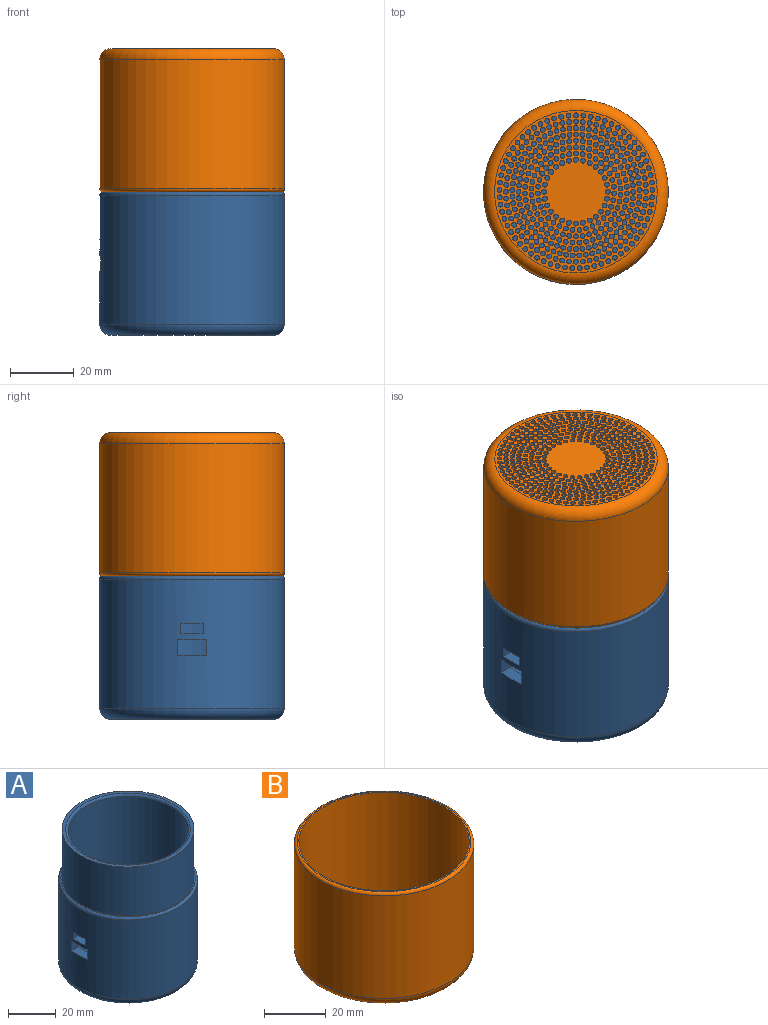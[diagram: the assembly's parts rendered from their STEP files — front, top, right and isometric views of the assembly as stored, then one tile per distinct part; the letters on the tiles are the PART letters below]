
ASSEMBLY  parts=2 mates=1
PART A: 18 faces, bbox 62.8x62.8x70 mm
  f0: cylinder r=29mm len=58mm, axis (0,0,-1), area 7312mm2, adj f6,f7,f8,f9,f10,f11,f12,f13
  f1: plane 55x55mm, normal (0,0,1), area 252.1mm2, adj f5,f15
  f2: cylinder r=25mm len=59mm, axis (0,0,1), area 9200mm2, adj f4,f5,f6,f7,f8,f9,f10,f11
  f3: plane 51x51mm, normal (0,0,-1), area 2042.8mm2, adj f17
  f4: plane 50x50mm, normal (0,0,1), area 1963.5mm2, adj f2
  f5: torus R=26mm, axis (0,0,1), area 250.3mm2, adj f1,f2
  f6: plane 9x4.41mm, normal (0,0,-1), area 36.2mm2, adj f0,f2,f7,f9
  f7: plane 5x4.06mm, normal (0,1,0), area 20.3mm2, adj f0,f2,f6,f8
  f8: plane 9x4.41mm, normal (0,0,1), area 36.2mm2, adj f0,f2,f7,f9
  f9: plane 5x4.06mm, normal (0,-1,0), area 20.3mm2, adj f0,f2,f6,f8
  f10: plane 4.03x3.2mm, normal (0,-1,0), area 12.9mm2, adj f0,f2,f11,f13
  f11: plane 7x4.25mm, normal (0,0,-1), area 28.1mm2, adj f0,f2,f10,f12
  f12: plane 4.03x3.2mm, normal (0,1,0), area 12.9mm2, adj f0,f2,f11,f13
  f13: plane 7x4.25mm, normal (0,0,1), area 28.1mm2, adj f0,f2,f10,f12
  f14: plane 56x56mm, normal (0,0,1), area 87.2mm2, adj f15,f16
  f15: cylinder r=27.5mm len=55mm, axis (0,0,1), area 4319.7mm2, adj f1,f14
  f16: torus R=28mm, axis (0,0,1), area 282.6mm2, adj f0,f14
  f17: torus R=25.5mm, axis (0,0,1), area 957.8mm2, adj f0,f3
PART B: 409 faces, bbox 62.8x62.8x45 mm
  f0: plane 51x51mm, normal (0,0,1), area 1339.5mm2, adj f6,f7,f8,f9,f10,f11,f12,f13
  f1: cylinder r=29mm len=58mm, axis (0,0,-1), area 7379.6mm2, adj f407,f408
  f2: plane 56x56mm, normal (0,0,1), area 87.2mm2, adj f4,f408
  f3: plane 51x51mm, normal (0,0,-1), area 1339.5mm2, adj f6,f7,f8,f9,f10,f11,f12,f13
  f4: cylinder r=27.5mm len=55mm, axis (0,0,1), area 6911.5mm2, adj f2,f5
  f5: plane 55x55mm, normal (0,0,1), area 43mm2, adj f4,f405
  f6: cylinder r=0.75mm len=5mm, axis (0,0,-1), area 23.6mm2, adj f0,f3
  f7: cylinder r=0.75mm len=5mm, axis (0,0,-1), area 23.6mm2, adj f0,f3
  f8: cylinder r=0.75mm len=5mm, axis (0,0,-1), area 23.6mm2, adj f0,f3
  f9: cylinder r=0.75mm len=5mm, axis (0,0,-1), area 23.6mm2, adj f0,f3
  f10: cylinder r=0.75mm len=5mm, axis (0,0,-1), area 23.6mm2, adj f0,f3
  f11: cylinder r=0.75mm len=5mm, axis (0,0,-1), area 23.6mm2, adj f0,f3
  f12: cylinder r=0.75mm len=5mm, axis (0,0,-1), area 23.6mm2, adj f0,f3
  f13: cylinder r=0.75mm len=5mm, axis (0,0,-1), area 23.6mm2, adj f0,f3
  f14: cylinder r=0.75mm len=5mm, axis (0,0,-1), area 23.6mm2, adj f0,f3
  f15: cylinder r=0.75mm len=5mm, axis (0,0,-1), area 23.6mm2, adj f0,f3
  f16: cylinder r=0.75mm len=5mm, axis (0,0,-1), area 23.6mm2, adj f0,f3
  f17: cylinder r=0.75mm len=5mm, axis (0,0,-1), area 23.6mm2, adj f0,f3
  f18: cylinder r=0.75mm len=5mm, axis (0,0,-1), area 23.6mm2, adj f0,f3
  f19: cylinder r=0.75mm len=5mm, axis (0,0,-1), area 23.6mm2, adj f0,f3
  f20: cylinder r=0.75mm len=5mm, axis (0,0,-1), area 23.6mm2, adj f0,f3
  f21: cylinder r=0.75mm len=5mm, axis (0,0,-1), area 23.6mm2, adj f0,f3
  f22: cylinder r=0.75mm len=5mm, axis (0,0,-1), area 23.6mm2, adj f0,f3
  f23: cylinder r=0.75mm len=5mm, axis (0,0,-1), area 23.6mm2, adj f0,f3
  f24: cylinder r=0.75mm len=5mm, axis (0,0,-1), area 23.6mm2, adj f0,f3
  f25: cylinder r=0.75mm len=5mm, axis (0,0,-1), area 23.6mm2, adj f0,f3
  f26: cylinder r=0.75mm len=5mm, axis (0,0,-1), area 23.6mm2, adj f0,f3
  f27: cylinder r=0.75mm len=5mm, axis (0,0,-1), area 23.6mm2, adj f0,f3
  f28: cylinder r=0.75mm len=5mm, axis (0,0,-1), area 23.6mm2, adj f0,f3
  f29: cylinder r=0.75mm len=5mm, axis (0,0,-1), area 23.6mm2, adj f0,f3
  f30: cylinder r=0.75mm len=5mm, axis (0,0,-1), area 23.6mm2, adj f0,f3
  f31: cylinder r=0.75mm len=5mm, axis (0,0,-1), area 23.6mm2, adj f0,f3
  f32: cylinder r=0.75mm len=5mm, axis (0,0,-1), area 23.6mm2, adj f0,f3
  f33: cylinder r=0.75mm len=5mm, axis (0,0,-1), area 23.6mm2, adj f0,f3
  f34: cylinder r=0.75mm len=5mm, axis (0,0,-1), area 23.6mm2, adj f0,f3
  f35: cylinder r=0.75mm len=5mm, axis (0,0,-1), area 23.6mm2, adj f0,f3
  f36: cylinder r=0.75mm len=5mm, axis (0,0,-1), area 23.6mm2, adj f0,f3
  f37: cylinder r=0.75mm len=5mm, axis (0,0,-1), area 23.6mm2, adj f0,f3
  f38: cylinder r=0.75mm len=5mm, axis (0,0,-1), area 23.6mm2, adj f0,f3
  f39: cylinder r=0.75mm len=5mm, axis (0,0,-1), area 23.6mm2, adj f0,f3
  f40: cylinder r=0.75mm len=5mm, axis (0,0,-1), area 23.6mm2, adj f0,f3
  f41: cylinder r=0.75mm len=5mm, axis (0,0,-1), area 23.6mm2, adj f0,f3
  f42: cylinder r=0.75mm len=5mm, axis (0,0,-1), area 23.6mm2, adj f0,f3
  f43: cylinder r=0.75mm len=5mm, axis (0,0,-1), area 23.6mm2, adj f0,f3
  f44: cylinder r=0.75mm len=5mm, axis (0,0,-1), area 23.6mm2, adj f0,f3
  f45: cylinder r=0.75mm len=5mm, axis (0,0,-1), area 23.6mm2, adj f0,f3
  f46: cylinder r=0.75mm len=5mm, axis (0,0,-1), area 23.6mm2, adj f0,f3
  f47: cylinder r=0.75mm len=5mm, axis (0,0,-1), area 23.6mm2, adj f0,f3
  f48: cylinder r=0.75mm len=5mm, axis (0,0,-1), area 23.6mm2, adj f0,f3
  f49: cylinder r=0.75mm len=5mm, axis (0,0,-1), area 23.6mm2, adj f0,f3
  f50: cylinder r=0.75mm len=5mm, axis (0,0,-1), area 23.6mm2, adj f0,f3
  f51: cylinder r=0.75mm len=5mm, axis (0,0,-1), area 23.6mm2, adj f0,f3
  f52: cylinder r=0.75mm len=5mm, axis (0,0,-1), area 23.6mm2, adj f0,f3
  f53: cylinder r=0.75mm len=5mm, axis (0,0,-1), area 23.6mm2, adj f0,f3
  f54: cylinder r=0.75mm len=5mm, axis (0,0,-1), area 23.6mm2, adj f0,f3
  f55: cylinder r=0.75mm len=5mm, axis (0,0,-1), area 23.6mm2, adj f0,f3
  f56: cylinder r=0.75mm len=5mm, axis (0,0,-1), area 23.6mm2, adj f0,f3
  f57: cylinder r=0.75mm len=5mm, axis (0,0,-1), area 23.6mm2, adj f0,f3
  f58: cylinder r=0.75mm len=5mm, axis (0,0,-1), area 23.6mm2, adj f0,f3
  f59: cylinder r=0.75mm len=5mm, axis (0,0,-1), area 23.6mm2, adj f0,f3
  f60: cylinder r=0.75mm len=5mm, axis (0,0,-1), area 23.6mm2, adj f0,f3
  f61: cylinder r=0.75mm len=5mm, axis (0,0,-1), area 23.6mm2, adj f0,f3
  f62: cylinder r=0.75mm len=5mm, axis (0,0,-1), area 23.6mm2, adj f0,f3
  f63: cylinder r=0.75mm len=5mm, axis (0,0,-1), area 23.6mm2, adj f0,f3
  f64: cylinder r=0.75mm len=5mm, axis (0,0,-1), area 23.6mm2, adj f0,f3
  f65: cylinder r=0.75mm len=5mm, axis (0,0,-1), area 23.6mm2, adj f0,f3
  f66: cylinder r=0.75mm len=5mm, axis (0,0,-1), area 23.6mm2, adj f0,f3
  f67: cylinder r=0.75mm len=5mm, axis (0,0,-1), area 23.6mm2, adj f0,f3
  f68: cylinder r=0.75mm len=5mm, axis (0,0,-1), area 23.6mm2, adj f0,f3
  f69: cylinder r=0.75mm len=5mm, axis (0,0,-1), area 23.6mm2, adj f0,f3
  f70: cylinder r=0.75mm len=5mm, axis (0,0,-1), area 23.6mm2, adj f0,f3
  f71: cylinder r=0.75mm len=5mm, axis (0,0,-1), area 23.6mm2, adj f0,f3
  f72: cylinder r=0.75mm len=5mm, axis (0,0,-1), area 23.6mm2, adj f0,f3
  f73: cylinder r=0.75mm len=5mm, axis (0,0,-1), area 23.6mm2, adj f0,f3
  f74: cylinder r=0.75mm len=5mm, axis (0,0,-1), area 23.6mm2, adj f0,f3
  f75: cylinder r=0.75mm len=5mm, axis (0,0,-1), area 23.6mm2, adj f0,f3
  f76: cylinder r=0.75mm len=5mm, axis (0,0,-1), area 23.6mm2, adj f0,f3
  f77: cylinder r=0.75mm len=5mm, axis (0,0,-1), area 23.6mm2, adj f0,f3
  f78: cylinder r=0.75mm len=5mm, axis (0,0,-1), area 23.6mm2, adj f0,f3
  f79: cylinder r=0.75mm len=5mm, axis (0,0,-1), area 23.6mm2, adj f0,f3
  f80: cylinder r=0.75mm len=5mm, axis (0,0,-1), area 23.6mm2, adj f0,f3
  f81: cylinder r=0.75mm len=5mm, axis (0,0,-1), area 23.6mm2, adj f0,f3
  f82: cylinder r=0.75mm len=5mm, axis (0,0,-1), area 23.6mm2, adj f0,f3
  f83: cylinder r=0.75mm len=5mm, axis (0,0,-1), area 23.6mm2, adj f0,f3
  f84: cylinder r=0.75mm len=5mm, axis (0,0,-1), area 23.6mm2, adj f0,f3
  f85: cylinder r=0.75mm len=5mm, axis (0,0,-1), area 23.6mm2, adj f0,f3
  f86: cylinder r=0.75mm len=5mm, axis (0,0,-1), area 23.6mm2, adj f0,f3
  f87: cylinder r=0.75mm len=5mm, axis (0,0,-1), area 23.6mm2, adj f0,f3
  f88: cylinder r=0.75mm len=5mm, axis (0,0,-1), area 23.6mm2, adj f0,f3
  f89: cylinder r=0.75mm len=5mm, axis (0,0,-1), area 23.6mm2, adj f0,f3
  f90: cylinder r=0.75mm len=5mm, axis (0,0,-1), area 23.6mm2, adj f0,f3
  f91: cylinder r=0.75mm len=5mm, axis (0,0,-1), area 23.6mm2, adj f0,f3
  f92: cylinder r=0.75mm len=5mm, axis (0,0,-1), area 23.6mm2, adj f0,f3
  f93: cylinder r=0.75mm len=5mm, axis (0,0,-1), area 23.6mm2, adj f0,f3
  f94: cylinder r=0.75mm len=5mm, axis (0,0,-1), area 23.6mm2, adj f0,f3
  f95: cylinder r=0.75mm len=5mm, axis (0,0,-1), area 23.6mm2, adj f0,f3
  f96: cylinder r=0.75mm len=5mm, axis (0,0,-1), area 23.6mm2, adj f0,f3
  f97: cylinder r=0.75mm len=5mm, axis (0,0,-1), area 23.6mm2, adj f0,f3
  f98: cylinder r=0.75mm len=5mm, axis (0,0,-1), area 23.6mm2, adj f0,f3
  f99: cylinder r=0.75mm len=5mm, axis (0,0,-1), area 23.6mm2, adj f0,f3
  f100: cylinder r=0.75mm len=5mm, axis (0,0,-1), area 23.6mm2, adj f0,f3
  f101: cylinder r=0.75mm len=5mm, axis (0,0,-1), area 23.6mm2, adj f0,f3
  f102: cylinder r=0.75mm len=5mm, axis (0,0,-1), area 23.6mm2, adj f0,f3
  f103: cylinder r=0.75mm len=5mm, axis (0,0,-1), area 23.6mm2, adj f0,f3
  f104: cylinder r=0.75mm len=5mm, axis (0,0,-1), area 23.6mm2, adj f0,f3
  f105: cylinder r=0.75mm len=5mm, axis (0,0,-1), area 23.6mm2, adj f0,f3
  f106: cylinder r=0.75mm len=5mm, axis (0,0,-1), area 23.6mm2, adj f0,f3
  f107: cylinder r=0.75mm len=5mm, axis (0,0,-1), area 23.6mm2, adj f0,f3
  f108: cylinder r=0.75mm len=5mm, axis (0,0,-1), area 23.6mm2, adj f0,f3
  f109: cylinder r=0.75mm len=5mm, axis (0,0,-1), area 23.6mm2, adj f0,f3
  f110: cylinder r=0.75mm len=5mm, axis (0,0,-1), area 23.6mm2, adj f0,f3
  f111: cylinder r=0.75mm len=5mm, axis (0,0,-1), area 23.6mm2, adj f0,f3
  f112: cylinder r=0.75mm len=5mm, axis (0,0,-1), area 23.6mm2, adj f0,f3
  f113: cylinder r=0.75mm len=5mm, axis (0,0,-1), area 23.6mm2, adj f0,f3
  f114: cylinder r=0.75mm len=5mm, axis (0,0,-1), area 23.6mm2, adj f0,f3
  f115: cylinder r=0.75mm len=5mm, axis (0,0,-1), area 23.6mm2, adj f0,f3
  f116: cylinder r=0.75mm len=5mm, axis (0,0,-1), area 23.6mm2, adj f0,f3
  f117: cylinder r=0.75mm len=5mm, axis (0,0,-1), area 23.6mm2, adj f0,f3
  f118: cylinder r=0.75mm len=5mm, axis (0,0,-1), area 23.6mm2, adj f0,f3
  f119: cylinder r=0.75mm len=5mm, axis (0,0,-1), area 23.6mm2, adj f0,f3
  f120: cylinder r=0.75mm len=5mm, axis (0,0,-1), area 23.6mm2, adj f0,f3
  f121: cylinder r=0.75mm len=5mm, axis (0,0,-1), area 23.6mm2, adj f0,f3
  f122: cylinder r=0.75mm len=5mm, axis (0,0,-1), area 23.6mm2, adj f0,f3
  f123: cylinder r=0.75mm len=5mm, axis (0,0,-1), area 23.6mm2, adj f0,f3
  f124: cylinder r=0.75mm len=5mm, axis (0,0,-1), area 23.6mm2, adj f0,f3
  f125: cylinder r=0.75mm len=5mm, axis (0,0,-1), area 23.6mm2, adj f0,f3
  f126: cylinder r=0.75mm len=5mm, axis (0,0,-1), area 23.6mm2, adj f0,f3
  f127: cylinder r=0.75mm len=5mm, axis (0,0,-1), area 23.6mm2, adj f0,f3
  f128: cylinder r=0.75mm len=5mm, axis (0,0,-1), area 23.6mm2, adj f0,f3
  f129: cylinder r=0.75mm len=5mm, axis (0,0,-1), area 23.6mm2, adj f0,f3
  f130: cylinder r=0.75mm len=5mm, axis (0,0,-1), area 23.6mm2, adj f0,f3
  f131: cylinder r=0.75mm len=5mm, axis (0,0,-1), area 23.6mm2, adj f0,f3
  f132: cylinder r=0.75mm len=5mm, axis (0,0,-1), area 23.6mm2, adj f0,f3
  f133: cylinder r=0.75mm len=5mm, axis (0,0,-1), area 23.6mm2, adj f0,f3
  f134: cylinder r=0.75mm len=5mm, axis (0,0,-1), area 23.6mm2, adj f0,f3
  f135: cylinder r=0.75mm len=5mm, axis (0,0,-1), area 23.6mm2, adj f0,f3
  f136: cylinder r=0.75mm len=5mm, axis (0,0,-1), area 23.6mm2, adj f0,f3
  f137: cylinder r=0.75mm len=5mm, axis (0,0,-1), area 23.6mm2, adj f0,f3
  f138: cylinder r=0.75mm len=5mm, axis (0,0,-1), area 23.6mm2, adj f0,f3
  f139: cylinder r=0.75mm len=5mm, axis (0,0,-1), area 23.6mm2, adj f0,f3
  f140: cylinder r=0.75mm len=5mm, axis (0,0,-1), area 23.6mm2, adj f0,f3
  f141: cylinder r=0.75mm len=5mm, axis (0,0,-1), area 23.6mm2, adj f0,f3
  f142: cylinder r=0.75mm len=5mm, axis (0,0,-1), area 23.6mm2, adj f0,f3
  f143: cylinder r=0.75mm len=5mm, axis (0,0,-1), area 23.6mm2, adj f0,f3
  f144: cylinder r=0.75mm len=5mm, axis (0,0,-1), area 23.6mm2, adj f0,f3
  f145: cylinder r=0.75mm len=5mm, axis (0,0,-1), area 23.6mm2, adj f0,f3
  f146: cylinder r=0.75mm len=5mm, axis (0,0,-1), area 23.6mm2, adj f0,f3
  f147: cylinder r=0.75mm len=5mm, axis (0,0,-1), area 23.6mm2, adj f0,f3
  f148: cylinder r=0.75mm len=5mm, axis (0,0,-1), area 23.6mm2, adj f0,f3
  f149: cylinder r=0.75mm len=5mm, axis (0,0,-1), area 23.6mm2, adj f0,f3
  f150: cylinder r=0.75mm len=5mm, axis (0,0,-1), area 23.6mm2, adj f0,f3
  f151: cylinder r=0.75mm len=5mm, axis (0,0,-1), area 23.6mm2, adj f0,f3
  f152: cylinder r=0.75mm len=5mm, axis (0,0,-1), area 23.6mm2, adj f0,f3
  f153: cylinder r=0.75mm len=5mm, axis (0,0,-1), area 23.6mm2, adj f0,f3
  f154: cylinder r=0.75mm len=5mm, axis (0,0,-1), area 23.6mm2, adj f0,f3
  f155: cylinder r=0.75mm len=5mm, axis (0,0,-1), area 23.6mm2, adj f0,f3
  f156: cylinder r=0.75mm len=5mm, axis (0,0,-1), area 23.6mm2, adj f0,f3
  f157: cylinder r=0.75mm len=5mm, axis (0,0,-1), area 23.6mm2, adj f0,f3
  f158: cylinder r=0.75mm len=5mm, axis (0,0,-1), area 23.6mm2, adj f0,f3
  f159: cylinder r=0.75mm len=5mm, axis (0,0,-1), area 23.6mm2, adj f0,f3
  f160: cylinder r=0.75mm len=5mm, axis (0,0,-1), area 23.6mm2, adj f0,f3
  f161: cylinder r=0.75mm len=5mm, axis (0,0,-1), area 23.6mm2, adj f0,f3
  f162: cylinder r=0.75mm len=5mm, axis (0,0,-1), area 23.6mm2, adj f0,f3
  f163: cylinder r=0.75mm len=5mm, axis (0,0,-1), area 23.6mm2, adj f0,f3
  f164: cylinder r=0.75mm len=5mm, axis (0,0,-1), area 23.6mm2, adj f0,f3
  f165: cylinder r=0.75mm len=5mm, axis (0,0,-1), area 23.6mm2, adj f0,f3
  f166: cylinder r=0.75mm len=5mm, axis (0,0,-1), area 23.6mm2, adj f0,f3
  f167: cylinder r=0.75mm len=5mm, axis (0,0,-1), area 23.6mm2, adj f0,f3
  f168: cylinder r=0.75mm len=5mm, axis (0,0,-1), area 23.6mm2, adj f0,f3
  f169: cylinder r=0.75mm len=5mm, axis (0,0,-1), area 23.6mm2, adj f0,f3
  f170: cylinder r=0.75mm len=5mm, axis (0,0,-1), area 23.6mm2, adj f0,f3
  f171: cylinder r=0.75mm len=5mm, axis (0,0,-1), area 23.6mm2, adj f0,f3
  f172: cylinder r=0.75mm len=5mm, axis (0,0,-1), area 23.6mm2, adj f0,f3
  f173: cylinder r=0.75mm len=5mm, axis (0,0,-1), area 23.6mm2, adj f0,f3
  f174: cylinder r=0.75mm len=5mm, axis (0,0,-1), area 23.6mm2, adj f0,f3
  f175: cylinder r=0.75mm len=5mm, axis (0,0,-1), area 23.6mm2, adj f0,f3
  f176: cylinder r=0.75mm len=5mm, axis (0,0,-1), area 23.6mm2, adj f0,f3
  f177: cylinder r=0.75mm len=5mm, axis (0,0,-1), area 23.6mm2, adj f0,f3
  f178: cylinder r=0.75mm len=5mm, axis (0,0,-1), area 23.6mm2, adj f0,f3
  f179: cylinder r=0.75mm len=5mm, axis (0,0,-1), area 23.6mm2, adj f0,f3
  f180: cylinder r=0.75mm len=5mm, axis (0,0,-1), area 23.6mm2, adj f0,f3
  f181: cylinder r=0.75mm len=5mm, axis (0,0,-1), area 23.6mm2, adj f0,f3
  f182: cylinder r=0.75mm len=5mm, axis (0,0,-1), area 23.6mm2, adj f0,f3
  f183: cylinder r=0.75mm len=5mm, axis (0,0,-1), area 23.6mm2, adj f0,f3
  f184: cylinder r=0.75mm len=5mm, axis (0,0,-1), area 23.6mm2, adj f0,f3
  f185: cylinder r=0.75mm len=5mm, axis (0,0,-1), area 23.6mm2, adj f0,f3
  f186: cylinder r=0.75mm len=5mm, axis (0,0,-1), area 23.6mm2, adj f0,f3
  f187: cylinder r=0.75mm len=5mm, axis (0,0,-1), area 23.6mm2, adj f0,f3
  f188: cylinder r=0.75mm len=5mm, axis (0,0,-1), area 23.6mm2, adj f0,f3
  f189: cylinder r=0.75mm len=5mm, axis (0,0,-1), area 23.6mm2, adj f0,f3
  f190: cylinder r=0.75mm len=5mm, axis (0,0,-1), area 23.6mm2, adj f0,f3
  f191: cylinder r=0.75mm len=5mm, axis (0,0,-1), area 23.6mm2, adj f0,f3
  f192: cylinder r=0.75mm len=5mm, axis (0,0,-1), area 23.6mm2, adj f0,f3
  f193: cylinder r=0.75mm len=5mm, axis (0,0,-1), area 23.6mm2, adj f0,f3
  f194: cylinder r=0.75mm len=5mm, axis (0,0,-1), area 23.6mm2, adj f0,f3
  f195: cylinder r=0.75mm len=5mm, axis (0,0,-1), area 23.6mm2, adj f0,f3
  f196: cylinder r=0.75mm len=5mm, axis (0,0,-1), area 23.6mm2, adj f0,f3
  f197: cylinder r=0.75mm len=5mm, axis (0,0,-1), area 23.6mm2, adj f0,f3
  f198: cylinder r=0.75mm len=5mm, axis (0,0,-1), area 23.6mm2, adj f0,f3
  f199: cylinder r=0.75mm len=5mm, axis (0,0,-1), area 23.6mm2, adj f0,f3
  f200: cylinder r=0.75mm len=5mm, axis (0,0,-1), area 23.6mm2, adj f0,f3
  f201: cylinder r=0.75mm len=5mm, axis (0,0,-1), area 23.6mm2, adj f0,f3
  f202: cylinder r=0.75mm len=5mm, axis (0,0,-1), area 23.6mm2, adj f0,f3
  f203: cylinder r=0.75mm len=5mm, axis (0,0,-1), area 23.6mm2, adj f0,f3
  f204: cylinder r=0.75mm len=5mm, axis (0,0,-1), area 23.6mm2, adj f0,f3
  f205: cylinder r=0.75mm len=5mm, axis (0,0,-1), area 23.6mm2, adj f0,f3
  f206: cylinder r=0.75mm len=5mm, axis (0,0,-1), area 23.6mm2, adj f0,f3
  f207: cylinder r=0.75mm len=5mm, axis (0,0,-1), area 23.6mm2, adj f0,f3
  f208: cylinder r=0.75mm len=5mm, axis (0,0,-1), area 23.6mm2, adj f0,f3
  f209: cylinder r=0.75mm len=5mm, axis (0,0,-1), area 23.6mm2, adj f0,f3
  f210: cylinder r=0.75mm len=5mm, axis (0,0,-1), area 23.6mm2, adj f0,f3
  f211: cylinder r=0.75mm len=5mm, axis (0,0,-1), area 23.6mm2, adj f0,f3
  f212: cylinder r=0.75mm len=5mm, axis (0,0,-1), area 23.6mm2, adj f0,f3
  f213: cylinder r=0.75mm len=5mm, axis (0,0,-1), area 23.6mm2, adj f0,f3
  f214: cylinder r=0.75mm len=5mm, axis (0,0,-1), area 23.6mm2, adj f0,f3
  f215: cylinder r=0.75mm len=5mm, axis (0,0,-1), area 23.6mm2, adj f0,f3
  f216: cylinder r=0.75mm len=5mm, axis (0,0,-1), area 23.6mm2, adj f0,f3
  f217: cylinder r=0.75mm len=5mm, axis (0,0,-1), area 23.6mm2, adj f0,f3
  f218: cylinder r=0.75mm len=5mm, axis (0,0,-1), area 23.6mm2, adj f0,f3
  f219: cylinder r=0.75mm len=5mm, axis (0,0,-1), area 23.6mm2, adj f0,f3
  f220: cylinder r=0.75mm len=5mm, axis (0,0,-1), area 23.6mm2, adj f0,f3
  f221: cylinder r=0.75mm len=5mm, axis (0,0,-1), area 23.6mm2, adj f0,f3
  f222: cylinder r=0.75mm len=5mm, axis (0,0,-1), area 23.6mm2, adj f0,f3
  f223: cylinder r=0.75mm len=5mm, axis (0,0,-1), area 23.6mm2, adj f0,f3
  f224: cylinder r=0.75mm len=5mm, axis (0,0,-1), area 23.6mm2, adj f0,f3
  f225: cylinder r=0.75mm len=5mm, axis (0,0,-1), area 23.6mm2, adj f0,f3
  f226: cylinder r=0.75mm len=5mm, axis (0,0,-1), area 23.6mm2, adj f0,f3
  f227: cylinder r=0.75mm len=5mm, axis (0,0,-1), area 23.6mm2, adj f0,f3
  f228: cylinder r=0.75mm len=5mm, axis (0,0,-1), area 23.6mm2, adj f0,f3
  f229: cylinder r=0.75mm len=5mm, axis (0,0,-1), area 23.6mm2, adj f0,f3
  f230: cylinder r=0.75mm len=5mm, axis (0,0,-1), area 23.6mm2, adj f0,f3
  f231: cylinder r=0.75mm len=5mm, axis (0,0,-1), area 23.6mm2, adj f0,f3
  f232: cylinder r=0.75mm len=5mm, axis (0,0,-1), area 23.6mm2, adj f0,f3
  f233: cylinder r=0.75mm len=5mm, axis (0,0,-1), area 23.6mm2, adj f0,f3
  f234: cylinder r=0.75mm len=5mm, axis (0,0,-1), area 23.6mm2, adj f0,f3
  f235: cylinder r=0.75mm len=5mm, axis (0,0,-1), area 23.6mm2, adj f0,f3
  f236: cylinder r=0.75mm len=5mm, axis (0,0,-1), area 23.6mm2, adj f0,f3
  f237: cylinder r=0.75mm len=5mm, axis (0,0,-1), area 23.6mm2, adj f0,f3
  f238: cylinder r=0.75mm len=5mm, axis (0,0,-1), area 23.6mm2, adj f0,f3
  f239: cylinder r=0.75mm len=5mm, axis (0,0,-1), area 23.6mm2, adj f0,f3
  f240: cylinder r=0.75mm len=5mm, axis (0,0,-1), area 23.6mm2, adj f0,f3
  f241: cylinder r=0.75mm len=5mm, axis (0,0,-1), area 23.6mm2, adj f0,f3
  f242: cylinder r=0.75mm len=5mm, axis (0,0,-1), area 23.6mm2, adj f0,f3
  f243: cylinder r=0.75mm len=5mm, axis (0,0,-1), area 23.6mm2, adj f0,f3
  f244: cylinder r=0.75mm len=5mm, axis (0,0,-1), area 23.6mm2, adj f0,f3
  f245: cylinder r=0.75mm len=5mm, axis (0,0,-1), area 23.6mm2, adj f0,f3
  f246: cylinder r=0.75mm len=5mm, axis (0,0,-1), area 23.6mm2, adj f0,f3
  f247: cylinder r=0.75mm len=5mm, axis (0,0,-1), area 23.6mm2, adj f0,f3
  f248: cylinder r=0.75mm len=5mm, axis (0,0,-1), area 23.6mm2, adj f0,f3
  f249: cylinder r=0.75mm len=5mm, axis (0,0,-1), area 23.6mm2, adj f0,f3
  f250: cylinder r=0.75mm len=5mm, axis (0,0,-1), area 23.6mm2, adj f0,f3
  f251: cylinder r=0.75mm len=5mm, axis (0,0,-1), area 23.6mm2, adj f0,f3
  f252: cylinder r=0.75mm len=5mm, axis (0,0,-1), area 23.6mm2, adj f0,f3
  f253: cylinder r=0.75mm len=5mm, axis (0,0,-1), area 23.6mm2, adj f0,f3
  f254: cylinder r=0.75mm len=5mm, axis (0,0,-1), area 23.6mm2, adj f0,f3
  f255: cylinder r=0.75mm len=5mm, axis (0,0,-1), area 23.6mm2, adj f0,f3
  f256: cylinder r=0.75mm len=5mm, axis (0,0,-1), area 23.6mm2, adj f0,f3
  f257: cylinder r=0.75mm len=5mm, axis (0,0,-1), area 23.6mm2, adj f0,f3
  f258: cylinder r=0.75mm len=5mm, axis (0,0,-1), area 23.6mm2, adj f0,f3
  f259: cylinder r=0.75mm len=5mm, axis (0,0,-1), area 23.6mm2, adj f0,f3
  f260: cylinder r=0.75mm len=5mm, axis (0,0,-1), area 23.6mm2, adj f0,f3
  f261: cylinder r=0.75mm len=5mm, axis (0,0,-1), area 23.6mm2, adj f0,f3
  f262: cylinder r=0.75mm len=5mm, axis (0,0,-1), area 23.6mm2, adj f0,f3
  f263: cylinder r=0.75mm len=5mm, axis (0,0,-1), area 23.6mm2, adj f0,f3
  f264: cylinder r=0.75mm len=5mm, axis (0,0,-1), area 23.6mm2, adj f0,f3
  f265: cylinder r=0.75mm len=5mm, axis (0,0,-1), area 23.6mm2, adj f0,f3
  f266: cylinder r=0.75mm len=5mm, axis (0,0,-1), area 23.6mm2, adj f0,f3
  f267: cylinder r=0.75mm len=5mm, axis (0,0,-1), area 23.6mm2, adj f0,f3
  f268: cylinder r=0.75mm len=5mm, axis (0,0,-1), area 23.6mm2, adj f0,f3
  f269: cylinder r=0.75mm len=5mm, axis (0,0,-1), area 23.6mm2, adj f0,f3
  f270: cylinder r=0.75mm len=5mm, axis (0,0,-1), area 23.6mm2, adj f0,f3
  f271: cylinder r=0.75mm len=5mm, axis (0,0,-1), area 23.6mm2, adj f0,f3
  f272: cylinder r=0.75mm len=5mm, axis (0,0,-1), area 23.6mm2, adj f0,f3
  f273: cylinder r=0.75mm len=5mm, axis (0,0,-1), area 23.6mm2, adj f0,f3
  f274: cylinder r=0.75mm len=5mm, axis (0,0,-1), area 23.6mm2, adj f0,f3
  f275: cylinder r=0.75mm len=5mm, axis (0,0,-1), area 23.6mm2, adj f0,f3
  f276: cylinder r=0.75mm len=5mm, axis (0,0,-1), area 23.6mm2, adj f0,f3
  f277: cylinder r=0.75mm len=5mm, axis (0,0,-1), area 23.6mm2, adj f0,f3
  f278: cylinder r=0.75mm len=5mm, axis (0,0,-1), area 23.6mm2, adj f0,f3
  f279: cylinder r=0.75mm len=5mm, axis (0,0,-1), area 23.6mm2, adj f0,f3
  f280: cylinder r=0.75mm len=5mm, axis (0,0,-1), area 23.6mm2, adj f0,f3
  f281: cylinder r=0.75mm len=5mm, axis (0,0,-1), area 23.6mm2, adj f0,f3
  f282: cylinder r=0.75mm len=5mm, axis (0,0,-1), area 23.6mm2, adj f0,f3
  f283: cylinder r=0.75mm len=5mm, axis (0,0,-1), area 23.6mm2, adj f0,f3
  f284: cylinder r=0.75mm len=5mm, axis (0,0,-1), area 23.6mm2, adj f0,f3
  f285: cylinder r=0.75mm len=5mm, axis (0,0,-1), area 23.6mm2, adj f0,f3
  f286: cylinder r=0.75mm len=5mm, axis (0,0,-1), area 23.6mm2, adj f0,f3
  f287: cylinder r=0.75mm len=5mm, axis (0,0,-1), area 23.6mm2, adj f0,f3
  f288: cylinder r=0.75mm len=5mm, axis (0,0,-1), area 23.6mm2, adj f0,f3
  f289: cylinder r=0.75mm len=5mm, axis (0,0,-1), area 23.6mm2, adj f0,f3
  f290: cylinder r=0.75mm len=5mm, axis (0,0,-1), area 23.6mm2, adj f0,f3
  f291: cylinder r=0.75mm len=5mm, axis (0,0,-1), area 23.6mm2, adj f0,f3
  f292: cylinder r=0.75mm len=5mm, axis (0,0,-1), area 23.6mm2, adj f0,f3
  f293: cylinder r=0.75mm len=5mm, axis (0,0,-1), area 23.6mm2, adj f0,f3
  f294: cylinder r=0.75mm len=5mm, axis (0,0,-1), area 23.6mm2, adj f0,f3
  f295: cylinder r=0.75mm len=5mm, axis (0,0,-1), area 23.6mm2, adj f0,f3
  f296: cylinder r=0.75mm len=5mm, axis (0,0,-1), area 23.6mm2, adj f0,f3
  f297: cylinder r=0.75mm len=5mm, axis (0,0,-1), area 23.6mm2, adj f0,f3
  f298: cylinder r=0.75mm len=5mm, axis (0,0,-1), area 23.6mm2, adj f0,f3
  f299: cylinder r=0.75mm len=5mm, axis (0,0,-1), area 23.6mm2, adj f0,f3
  f300: cylinder r=0.75mm len=5mm, axis (0,0,-1), area 23.6mm2, adj f0,f3
  f301: cylinder r=0.75mm len=5mm, axis (0,0,-1), area 23.6mm2, adj f0,f3
  f302: cylinder r=0.75mm len=5mm, axis (0,0,-1), area 23.6mm2, adj f0,f3
  f303: cylinder r=0.75mm len=5mm, axis (0,0,-1), area 23.6mm2, adj f0,f3
  f304: cylinder r=0.75mm len=5mm, axis (0,0,-1), area 23.6mm2, adj f0,f3
  f305: cylinder r=0.75mm len=5mm, axis (0,0,-1), area 23.6mm2, adj f0,f3
  f306: cylinder r=0.75mm len=5mm, axis (0,0,-1), area 23.6mm2, adj f0,f3
  f307: cylinder r=0.75mm len=5mm, axis (0,0,-1), area 23.6mm2, adj f0,f3
  f308: cylinder r=0.75mm len=5mm, axis (0,0,-1), area 23.6mm2, adj f0,f3
  f309: cylinder r=0.75mm len=5mm, axis (0,0,-1), area 23.6mm2, adj f0,f3
  f310: cylinder r=0.75mm len=5mm, axis (0,0,-1), area 23.6mm2, adj f0,f3
  f311: cylinder r=0.75mm len=5mm, axis (0,0,-1), area 23.6mm2, adj f0,f3
  f312: cylinder r=0.75mm len=5mm, axis (0,0,-1), area 23.6mm2, adj f0,f3
  f313: cylinder r=0.75mm len=5mm, axis (0,0,-1), area 23.6mm2, adj f0,f3
  f314: cylinder r=0.75mm len=5mm, axis (0,0,-1), area 23.6mm2, adj f0,f3
  f315: cylinder r=0.75mm len=5mm, axis (0,0,-1), area 23.6mm2, adj f0,f3
  f316: cylinder r=0.75mm len=5mm, axis (0,0,-1), area 23.6mm2, adj f0,f3
  f317: cylinder r=0.75mm len=5mm, axis (0,0,-1), area 23.6mm2, adj f0,f3
  f318: cylinder r=0.75mm len=5mm, axis (0,0,-1), area 23.6mm2, adj f0,f3
  f319: cylinder r=0.75mm len=5mm, axis (0,0,-1), area 23.6mm2, adj f0,f3
  f320: cylinder r=0.75mm len=5mm, axis (0,0,-1), area 23.6mm2, adj f0,f3
  f321: cylinder r=0.75mm len=5mm, axis (0,0,-1), area 23.6mm2, adj f0,f3
  f322: cylinder r=0.75mm len=5mm, axis (0,0,-1), area 23.6mm2, adj f0,f3
  f323: cylinder r=0.75mm len=5mm, axis (0,0,-1), area 23.6mm2, adj f0,f3
  f324: cylinder r=0.75mm len=5mm, axis (0,0,-1), area 23.6mm2, adj f0,f3
  f325: cylinder r=0.75mm len=5mm, axis (0,0,-1), area 23.6mm2, adj f0,f3
  f326: cylinder r=0.75mm len=5mm, axis (0,0,-1), area 23.6mm2, adj f0,f3
  f327: cylinder r=0.75mm len=5mm, axis (0,0,-1), area 23.6mm2, adj f0,f3
  f328: cylinder r=0.75mm len=5mm, axis (0,0,-1), area 23.6mm2, adj f0,f3
  f329: cylinder r=0.75mm len=5mm, axis (0,0,-1), area 23.6mm2, adj f0,f3
  f330: cylinder r=0.75mm len=5mm, axis (0,0,-1), area 23.6mm2, adj f0,f3
  f331: cylinder r=0.75mm len=5mm, axis (0,0,-1), area 23.6mm2, adj f0,f3
  f332: cylinder r=0.75mm len=5mm, axis (0,0,-1), area 23.6mm2, adj f0,f3
  f333: cylinder r=0.75mm len=5mm, axis (0,0,-1), area 23.6mm2, adj f0,f3
  f334: cylinder r=0.75mm len=5mm, axis (0,0,-1), area 23.6mm2, adj f0,f3
  f335: cylinder r=0.75mm len=5mm, axis (0,0,-1), area 23.6mm2, adj f0,f3
  f336: cylinder r=0.75mm len=5mm, axis (0,0,-1), area 23.6mm2, adj f0,f3
  f337: cylinder r=0.75mm len=5mm, axis (0,0,-1), area 23.6mm2, adj f0,f3
  f338: cylinder r=0.75mm len=5mm, axis (0,0,-1), area 23.6mm2, adj f0,f3
  f339: cylinder r=0.75mm len=5mm, axis (0,0,-1), area 23.6mm2, adj f0,f3
  f340: cylinder r=0.75mm len=5mm, axis (0,0,-1), area 23.6mm2, adj f0,f3
  f341: cylinder r=0.75mm len=5mm, axis (0,0,-1), area 23.6mm2, adj f0,f3
  f342: cylinder r=0.75mm len=5mm, axis (0,0,-1), area 23.6mm2, adj f0,f3
  f343: cylinder r=0.75mm len=5mm, axis (0,0,-1), area 23.6mm2, adj f0,f3
  f344: cylinder r=0.75mm len=5mm, axis (0,0,-1), area 23.6mm2, adj f0,f3
  f345: cylinder r=0.75mm len=5mm, axis (0,0,-1), area 23.6mm2, adj f0,f3
  f346: cylinder r=0.75mm len=5mm, axis (0,0,-1), area 23.6mm2, adj f0,f3
  f347: cylinder r=0.75mm len=5mm, axis (0,0,-1), area 23.6mm2, adj f0,f3
  f348: cylinder r=0.75mm len=5mm, axis (0,0,-1), area 23.6mm2, adj f0,f3
  f349: cylinder r=0.75mm len=5mm, axis (0,0,-1), area 23.6mm2, adj f0,f3
  f350: cylinder r=0.75mm len=5mm, axis (0,0,-1), area 23.6mm2, adj f0,f3
  f351: cylinder r=0.75mm len=5mm, axis (0,0,-1), area 23.6mm2, adj f0,f3
  f352: cylinder r=0.75mm len=5mm, axis (0,0,-1), area 23.6mm2, adj f0,f3
  f353: cylinder r=0.75mm len=5mm, axis (0,0,-1), area 23.6mm2, adj f0,f3
  f354: cylinder r=0.75mm len=5mm, axis (0,0,-1), area 23.6mm2, adj f0,f3
  f355: cylinder r=0.75mm len=5mm, axis (0,0,-1), area 23.6mm2, adj f0,f3
  f356: cylinder r=0.75mm len=5mm, axis (0,0,-1), area 23.6mm2, adj f0,f3
  f357: cylinder r=0.75mm len=5mm, axis (0,0,-1), area 23.6mm2, adj f0,f3
  f358: cylinder r=0.75mm len=5mm, axis (0,0,-1), area 23.6mm2, adj f0,f3
  f359: cylinder r=0.75mm len=5mm, axis (0,0,-1), area 23.6mm2, adj f0,f3
  f360: cylinder r=0.75mm len=5mm, axis (0,0,-1), area 23.6mm2, adj f0,f3
  f361: cylinder r=0.75mm len=5mm, axis (0,0,-1), area 23.6mm2, adj f0,f3
  f362: cylinder r=0.75mm len=5mm, axis (0,0,-1), area 23.6mm2, adj f0,f3
  f363: cylinder r=0.75mm len=5mm, axis (0,0,-1), area 23.6mm2, adj f0,f3
  f364: cylinder r=0.75mm len=5mm, axis (0,0,-1), area 23.6mm2, adj f0,f3
  f365: cylinder r=0.75mm len=5mm, axis (0,0,-1), area 23.6mm2, adj f0,f3
  f366: cylinder r=0.75mm len=5mm, axis (0,0,-1), area 23.6mm2, adj f0,f3
  f367: cylinder r=0.75mm len=5mm, axis (0,0,-1), area 23.6mm2, adj f0,f3
  f368: cylinder r=0.75mm len=5mm, axis (0,0,-1), area 23.6mm2, adj f0,f3
  f369: cylinder r=0.75mm len=5mm, axis (0,0,-1), area 23.6mm2, adj f0,f3
  f370: cylinder r=0.75mm len=5mm, axis (0,0,-1), area 23.6mm2, adj f0,f3
  f371: cylinder r=0.75mm len=5mm, axis (0,0,-1), area 23.6mm2, adj f0,f3
  f372: cylinder r=0.75mm len=5mm, axis (0,0,-1), area 23.6mm2, adj f0,f3
  f373: cylinder r=0.75mm len=5mm, axis (0,0,-1), area 23.6mm2, adj f0,f3
  f374: cylinder r=0.75mm len=5mm, axis (0,0,-1), area 23.6mm2, adj f0,f3
  f375: cylinder r=0.75mm len=5mm, axis (0,0,-1), area 23.6mm2, adj f0,f3
  f376: cylinder r=0.75mm len=5mm, axis (0,0,-1), area 23.6mm2, adj f0,f3
  f377: cylinder r=0.75mm len=5mm, axis (0,0,-1), area 23.6mm2, adj f0,f3
  f378: cylinder r=0.75mm len=5mm, axis (0,0,-1), area 23.6mm2, adj f0,f3
  f379: cylinder r=0.75mm len=5mm, axis (0,0,-1), area 23.6mm2, adj f0,f3
  f380: cylinder r=0.75mm len=5mm, axis (0,0,-1), area 23.6mm2, adj f0,f3
  f381: cylinder r=0.75mm len=5mm, axis (0,0,-1), area 23.6mm2, adj f0,f3
  f382: cylinder r=0.75mm len=5mm, axis (0,0,-1), area 23.6mm2, adj f0,f3
  f383: cylinder r=0.75mm len=5mm, axis (0,0,-1), area 23.6mm2, adj f0,f3
  f384: cylinder r=0.75mm len=5mm, axis (0,0,-1), area 23.6mm2, adj f0,f3
  f385: cylinder r=0.75mm len=5mm, axis (0,0,-1), area 23.6mm2, adj f0,f3
  f386: cylinder r=0.75mm len=5mm, axis (0,0,-1), area 23.6mm2, adj f0,f3
  f387: cylinder r=0.75mm len=5mm, axis (0,0,-1), area 23.6mm2, adj f0,f3
  f388: cylinder r=0.75mm len=5mm, axis (0,0,-1), area 23.6mm2, adj f0,f3
  f389: cylinder r=0.75mm len=5mm, axis (0,0,-1), area 23.6mm2, adj f0,f3
  f390: cylinder r=0.75mm len=5mm, axis (0,0,-1), area 23.6mm2, adj f0,f3
  f391: cylinder r=0.75mm len=5mm, axis (0,0,-1), area 23.6mm2, adj f0,f3
  f392: cylinder r=0.75mm len=5mm, axis (0,0,-1), area 23.6mm2, adj f0,f3
  f393: cylinder r=0.75mm len=5mm, axis (0,0,-1), area 23.6mm2, adj f0,f3
  f394: cylinder r=0.75mm len=5mm, axis (0,0,-1), area 23.6mm2, adj f0,f3
  f395: cylinder r=0.75mm len=5mm, axis (0,0,-1), area 23.6mm2, adj f0,f3
  f396: cylinder r=0.75mm len=5mm, axis (0,0,-1), area 23.6mm2, adj f0,f3
  f397: cylinder r=0.75mm len=5mm, axis (0,0,-1), area 23.6mm2, adj f0,f3
  f398: cylinder r=0.75mm len=5mm, axis (0,0,-1), area 23.6mm2, adj f0,f3
  f399: cylinder r=0.75mm len=5mm, axis (0,0,-1), area 23.6mm2, adj f0,f3
  f400: cylinder r=0.75mm len=5mm, axis (0,0,-1), area 23.6mm2, adj f0,f3
  f401: cylinder r=0.75mm len=5mm, axis (0,0,-1), area 23.6mm2, adj f0,f3
  f402: cylinder r=0.75mm len=5mm, axis (0,0,-1), area 23.6mm2, adj f0,f3
  f403: cylinder r=0.75mm len=5mm, axis (0,0,-1), area 23.6mm2, adj f0,f3
  f404: cylinder r=25.5mm len=51mm, axis (0,0,1), area 640.9mm2, adj f0,f406
  f405: cylinder r=27.25mm len=54.5mm, axis (0,0,1), area 684.9mm2, adj f5,f406
  f406: plane 54.5x54.5mm, normal (0,0,1), area 290mm2, adj f404,f405
  f407: torus R=25.5mm, axis (0,0,1), area 957.8mm2, adj f1,f3
  f408: torus R=28mm, axis (0,0,1), area 282.6mm2, adj f1,f2
PLACE A t=(93.48,10.06,-60.09)mm
PLACE B rot(axis=(-1,0,0),180deg) t=(93.48,10.06,29.91)mm
MATE fastened B.f405 <-> A.f2  axis (0,0,-1) through (93.48,10.06,-15.09)mm
